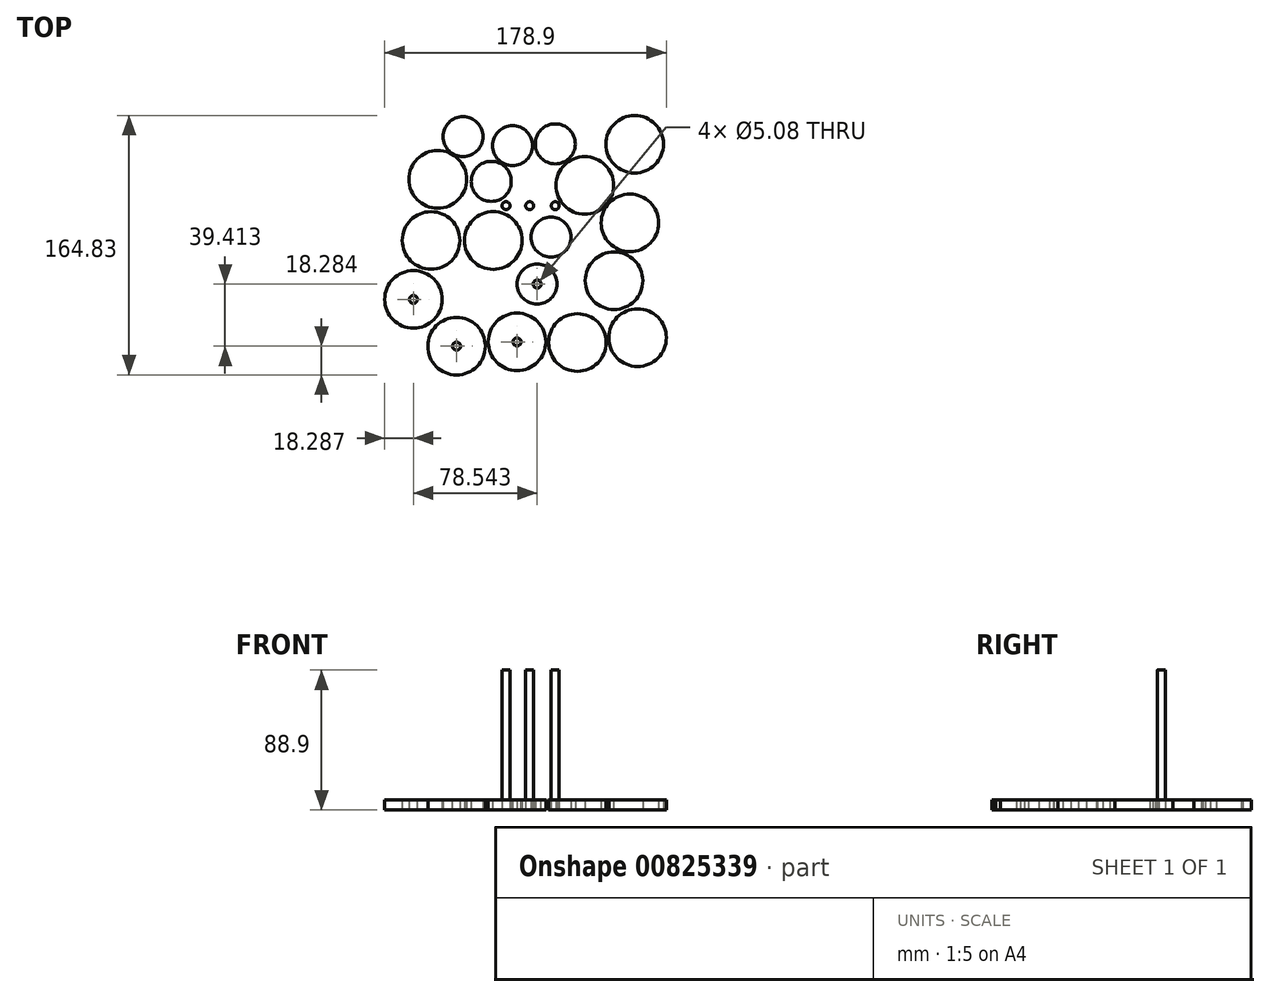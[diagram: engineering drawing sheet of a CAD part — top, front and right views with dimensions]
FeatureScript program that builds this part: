
annotation { "Feature Type Name" : "Feature", "Feature Type Description" : "" }
export const myFeature = defineFeature(function(context is Context, id is Id, definition is map)
    precondition{}
    {
        {
            var Q0;
            Q0=qCreatedBy(makeId("Top.planeOp"),FACE);
            var sketch = newSketch(context, id + "F0", { "sketchPlane" : qUnion([Q0])});
            skCircle(sketch, "E0", {"center": v(-40.84, 25.53) * mm, "radius": 2.54 * mm});
            skSolve(sketch);
        }
        {
            var Q0;
            Q0 = qSketchRegion(id + "F0", true);
            extrude(context, id + "F1", {"entities" : qUnion([Q0]), "depth" : 88.9 * mm, "offsetDistance" : 25.4 * mm});
        }
        {
            var Q0;
            Q0=makeQuery(id+"F1.opExtrude","SWEPT_BODY",BODY,{"disambiguationData":[OSD([sQuery(id+"F0.wireOp",EDGE,"E0")])]});
            transform(context, id + "F2", {"entities" : qUnion([Q0]), "transformType" : TransformType.TRANSLATION_3D, "dx" : 21.08 * mm, "dy" : 0 * mm, "dz" : 0 * mm, "makeCopy" : false});
        }
        {
            var Q0;
            Q0=makeQuery(id+"F1.opExtrude","SWEPT_BODY",BODY,{"disambiguationData":[OSD([sQuery(id+"F0.wireOp",EDGE,"E0")])]});
            transform(context, id + "F3", {"entities" : qUnion([Q0]), "transformType" : TransformType.TRANSLATION_3D, "dx" : 15 * mm, "dy" : 0 * mm, "dz" : 0 * mm, "makeCopy" : true});
        }
        {
            var Q0;
            Q0=makeQuery(id+"F3.opPattern","COPY",BODY,{"derivedFrom":makeQuery(id+"F1.opExtrude","SWEPT_BODY",BODY,{"disambiguationData":[OSD([sQuery(id+"F0.wireOp",EDGE,"E0")])]}),"instanceName":"1"});
            transform(context, id + "F4", {"entities" : qUnion([Q0]), "transformType" : TransformType.TRANSLATION_3D, "dx" : 16.26 * mm, "dy" : 0 * mm, "dz" : 0 * mm, "makeCopy" : true});
        }
        {
            var Q0;
            Q0=qCreatedBy(makeId("Top.planeOp"),FACE);
            var sketch = newSketch(context, id + "F5", { "sketchPlane" : qUnion([Q0])});
            skCircle(sketch, "E1", {"center": v(-51.16, -63.66) * mm, "radius": 18.29 * mm});
            skCircle(sketch, "E2", {"center": v(-12.78, -60.96) * mm, "radius": 18.29 * mm});
            skCircle(sketch, "E3", {"center": v(25.6, -61.34) * mm, "radius": 18.29 * mm});
            skCircle(sketch, "E4", {"center": v(63.78, -58.26) * mm, "radius": 18.29 * mm});
            skCircle(sketch, "E5", {"center": v(-67.36, 3.46) * mm, "radius": 18.29 * mm});
            skCircle(sketch, "E6", {"center": v(-78.54, -33.96) * mm, "radius": 18.29 * mm});
            skCircle(sketch, "E7", {"center": v(0, -24.24) * mm, "radius": 12.7 * mm});
            skCircle(sketch, "E8", {"center": v(48.85, -22.09) * mm, "radius": 18.29 * mm});
            skCircle(sketch, "E9", {"center": v(58.94, 14.6) * mm, "radius": 18.29 * mm});
            skCircle(sketch, "E10", {"center": v(-27.82, 3.46) * mm, "radius": 18.34 * mm});
            skCircle(sketch, "E11", {"center": v(-63.14, 42.3) * mm, "radius": 18.34 * mm});
            skCircle(sketch, "E12", {"center": v(-47.1, 69.4) * mm, "radius": 12.7 * mm});
            skCircle(sketch, "E13", {"center": v(-15.58, 63.7) * mm, "radius": 12.7 * mm});
            skCircle(sketch, "E14", {"center": v(11.52, 64.8) * mm, "radius": 12.7 * mm});
            skCircle(sketch, "E15", {"center": v(61.92, 64.6) * mm, "radius": 18.29 * mm});
            skCircle(sketch, "E16", {"center": v(-29.13, 40.98) * mm, "radius": 12.7 * mm});
            skCircle(sketch, "E17", {"center": v(30.27, 38.46) * mm, "radius": 18.29 * mm});
            skCircle(sketch, "E18", {"center": v(8.82, 5.58) * mm, "radius": 12.7 * mm});
            skSolve(sketch);
        }
        {
            var Q0;
            Q0=makeQuery(id+"F5.imprint","IMPRINT",FACE,{"disambiguationData":[TD([[makeQuery(id+"F5.imprint","IMPRINT",EDGE,{"derivedFrom":sQuery(id+"F5.wireOp",EDGE,"E12")}),1.0]])]});
            var Q1;
            Q1=makeQuery(id+"F5.imprint","IMPRINT",FACE,{"disambiguationData":[TD([[makeQuery(id+"F5.imprint","IMPRINT",EDGE,{"derivedFrom":sQuery(id+"F5.wireOp",EDGE,"E11")}),1.0]])]});
            var Q2;
            Q2=makeQuery(id+"F5.imprint","IMPRINT",FACE,{"disambiguationData":[TD([[makeQuery(id+"F5.imprint","IMPRINT",EDGE,{"derivedFrom":sQuery(id+"F5.wireOp",EDGE,"E10")}),1.0]])]});
            var Q3;
            Q3=makeQuery(id+"F5.imprint","IMPRINT",FACE,{"disambiguationData":[TD([[makeQuery(id+"F5.imprint","IMPRINT",EDGE,{"derivedFrom":sQuery(id+"F5.wireOp",EDGE,"E5")}),1.0]])]});
            var Q4;
            Q4=makeQuery(id+"F5.imprint","IMPRINT",FACE,{"disambiguationData":[TD([[makeQuery(id+"F5.imprint","IMPRINT",EDGE,{"derivedFrom":sQuery(id+"F5.wireOp",EDGE,"E1")}),1.0]])]});
            var Q5;
            Q5=makeQuery(id+"F5.imprint","IMPRINT",FACE,{"disambiguationData":[TD([[makeQuery(id+"F5.imprint","IMPRINT",EDGE,{"derivedFrom":sQuery(id+"F5.wireOp",EDGE,"E2")}),1.0]])]});
            var Q6;
            Q6=makeQuery(id+"F5.imprint","IMPRINT",FACE,{"disambiguationData":[TD([[makeQuery(id+"F5.imprint","IMPRINT",EDGE,{"derivedFrom":sQuery(id+"F5.wireOp",EDGE,"E6")}),1.0]])]});
            var Q7;
            Q7=makeQuery(id+"F5.imprint","IMPRINT",FACE,{"disambiguationData":[TD([[makeQuery(id+"F5.imprint","IMPRINT",EDGE,{"derivedFrom":sQuery(id+"F5.wireOp",EDGE,"E18")}),1.0]])]});
            var Q8;
            Q8=makeQuery(id+"F5.imprint","IMPRINT",FACE,{"disambiguationData":[TD([[makeQuery(id+"F5.imprint","IMPRINT",EDGE,{"derivedFrom":sQuery(id+"F5.wireOp",EDGE,"E13")}),1.0]])]});
            var Q9;
            Q9=makeQuery(id+"F5.imprint","IMPRINT",FACE,{"disambiguationData":[TD([[makeQuery(id+"F5.imprint","IMPRINT",EDGE,{"derivedFrom":sQuery(id+"F5.wireOp",EDGE,"E14")}),1.0]])]});
            var Q10;
            Q10=makeQuery(id+"F5.imprint","IMPRINT",FACE,{"disambiguationData":[TD([[makeQuery(id+"F5.imprint","IMPRINT",EDGE,{"derivedFrom":sQuery(id+"F5.wireOp",EDGE,"E15")}),1.0]])]});
            var Q11;
            Q11=makeQuery(id+"F5.imprint","IMPRINT",FACE,{"disambiguationData":[TD([[makeQuery(id+"F5.imprint","IMPRINT",EDGE,{"derivedFrom":sQuery(id+"F5.wireOp",EDGE,"E16")}),1.0]])]});
            var Q12;
            Q12=makeQuery(id+"F5.imprint","IMPRINT",FACE,{"disambiguationData":[TD([[makeQuery(id+"F5.imprint","IMPRINT",EDGE,{"derivedFrom":sQuery(id+"F5.wireOp",EDGE,"E17")}),1.0]])]});
            var Q13;
            Q13=makeQuery(id+"F5.imprint","IMPRINT",FACE,{"disambiguationData":[TD([[makeQuery(id+"F5.imprint","IMPRINT",EDGE,{"derivedFrom":sQuery(id+"F5.wireOp",EDGE,"E9")}),1.0]])]});
            var Q14;
            Q14=makeQuery(id+"F5.imprint","IMPRINT",FACE,{"disambiguationData":[TD([[makeQuery(id+"F5.imprint","IMPRINT",EDGE,{"derivedFrom":sQuery(id+"F5.wireOp",EDGE,"E8")}),1.0]])]});
            var Q15;
            Q15=makeQuery(id+"F5.imprint","IMPRINT",FACE,{"disambiguationData":[TD([[makeQuery(id+"F5.imprint","IMPRINT",EDGE,{"derivedFrom":sQuery(id+"F5.wireOp",EDGE,"E7")}),1.0]])]});
            var Q16;
            Q16=makeQuery(id+"F5.imprint","IMPRINT",FACE,{"disambiguationData":[TD([[makeQuery(id+"F5.imprint","IMPRINT",EDGE,{"derivedFrom":sQuery(id+"F5.wireOp",EDGE,"E3")}),1.0]])]});
            var Q17;
            Q17=makeQuery(id+"F5.imprint","IMPRINT",FACE,{"disambiguationData":[TD([[makeQuery(id+"F5.imprint","IMPRINT",EDGE,{"derivedFrom":sQuery(id+"F5.wireOp",EDGE,"E4")}),1.0]])]});
            extrude(context, id + "F6", {"entities" : qUnion([Q0, Q1, Q2, Q3, Q4, Q5, Q6, Q7, Q8, Q9, Q10, Q11, Q12, Q13, Q14, Q15, Q16, Q17]), "depth" : 6.35 * mm, "offsetDistance" : 25.4 * mm});
        }
        {
            var Q0;
            Q0=makeQuery(id+"F6.opExtrude","CAP_FACE",FACE,{"disambiguationData":[OSD([sQuery(id+"F5.wireOp",EDGE,"E1")])],"isStart":false});
            var sketch = newSketch(context, id + "F7", { "sketchPlane" : qUnion([Q0])});
            skCircle(sketch, "E19", {"center": v(-51.16, -63.66) * mm, "radius": 2.54 * mm});
            skSolve(sketch);
        }
        {
            var Q0;
            Q0=makeQuery(id+"F6.opExtrude","CAP_FACE",FACE,{"disambiguationData":[OSD([sQuery(id+"F5.wireOp",EDGE,"E2")])],"isStart":false});
            var sketch = newSketch(context, id + "F8", { "sketchPlane" : qUnion([Q0])});
            skCircle(sketch, "E20", {"center": v(-12.78, -60.96) * mm, "radius": 2.54 * mm});
            skSolve(sketch);
        }
        {
            var Q0;
            Q0=makeQuery(id+"F6.opExtrude","CAP_FACE",FACE,{"disambiguationData":[OSD([sQuery(id+"F5.wireOp",EDGE,"E6")])],"isStart":false});
            var sketch = newSketch(context, id + "F9", { "sketchPlane" : qUnion([Q0])});
            skCircle(sketch, "E21", {"center": v(-78.54, -33.96) * mm, "radius": 2.54 * mm});
            skSolve(sketch);
        }
        {
            var Q0;
            Q0=makeQuery(id+"F9.imprint","IMPRINT",FACE,{"disambiguationData":[TD([[makeQuery(id+"F9.imprint","IMPRINT",EDGE,{"derivedFrom":sQuery(id+"F9.wireOp",EDGE,"E21")}),1.0]])]});
            extrude(context, id + "F10", {"entities" : qUnion([Q0]), "operationType" : NewBodyOperationType.REMOVE, "oppositeDirection" : true, "depth" : 25.4 * mm, "offsetDistance" : 25.4 * mm});
        }
        {
            var Q0;
            Q0=makeQuery(id+"F7.imprint","IMPRINT",FACE,{"disambiguationData":[TD([[makeQuery(id+"F7.imprint","IMPRINT",EDGE,{"derivedFrom":sQuery(id+"F7.wireOp",EDGE,"E19")}),1.0]])]});
            extrude(context, id + "F11", {"entities" : qUnion([Q0]), "operationType" : NewBodyOperationType.REMOVE, "oppositeDirection" : true, "depth" : 25.4 * mm, "offsetDistance" : 25.4 * mm});
        }
        {
            var Q0;
            Q0=makeQuery(id+"F8.imprint","IMPRINT",FACE,{"disambiguationData":[TD([[makeQuery(id+"F8.imprint","IMPRINT",EDGE,{"derivedFrom":sQuery(id+"F8.wireOp",EDGE,"E20")}),1.0]])]});
            extrude(context, id + "F12", {"entities" : qUnion([Q0]), "operationType" : NewBodyOperationType.REMOVE, "oppositeDirection" : true, "depth" : 25.4 * mm, "offsetDistance" : 25.4 * mm});
        }
        {
            var Q0;
            Q0=makeQuery(id+"F6.opExtrude","CAP_FACE",FACE,{"disambiguationData":[OSD([sQuery(id+"F5.wireOp",EDGE,"E7")])],"isStart":false});
            var sketch = newSketch(context, id + "F13", { "sketchPlane" : qUnion([Q0])});
            skCircle(sketch, "E22", {"center": v(0, -24.24) * mm, "radius": 2.54 * mm});
            skSolve(sketch);
        }
        {
            var Q0;
            Q0 = qSketchRegion(id + "F13", true);
            extrude(context, id + "F14", {"entities" : qUnion([Q0]), "operationType" : NewBodyOperationType.REMOVE, "oppositeDirection" : true, "depth" : 25.4 * mm, "offsetDistance" : 25.4 * mm});
        }
    });
